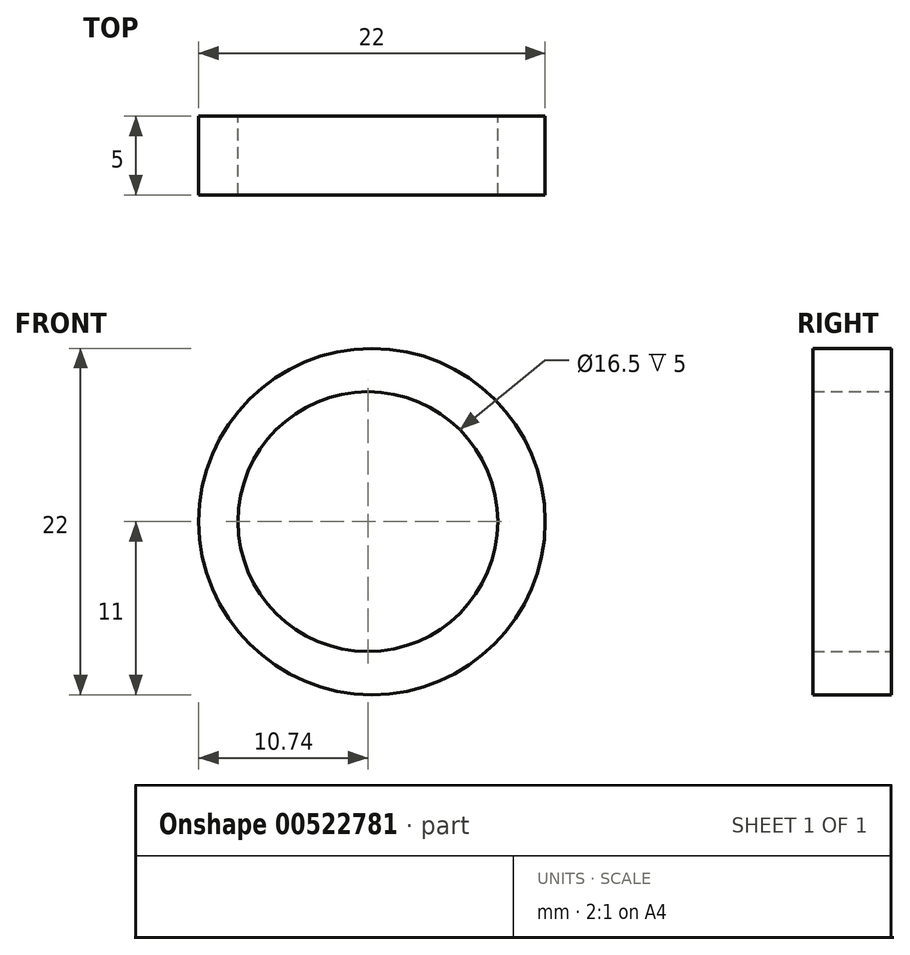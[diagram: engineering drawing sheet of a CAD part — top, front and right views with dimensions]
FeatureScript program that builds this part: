
annotation { "Feature Type Name" : "Feature", "Feature Type Description" : "" }
export const myFeature = defineFeature(function(context is Context, id is Id, definition is map)
    precondition{}
    {
        {
            var Q0;
            Q0=qCreatedBy(makeId("Front.planeOp"),FACE);
            var sketch = newSketch(context, id + "F0", { "sketchPlane" : qUnion([Q0])});
            skCircle(sketch, "E0", {"center": v(0.26, 0) * mm, "radius": 11 * mm});
            skCircle(sketch, "E1", {"center": v(0, 0) * mm, "radius": 8.25 * mm});
            skSolve(sketch);
        }
        {
            var Q0;
            Q0 = qSketchRegion(id + "F0", true);
            extrude(context, id + "F1", {"entities" : qUnion([Q0]), "depth" : 5 * mm, "offsetDistance" : 25 * mm});
        }
    });
